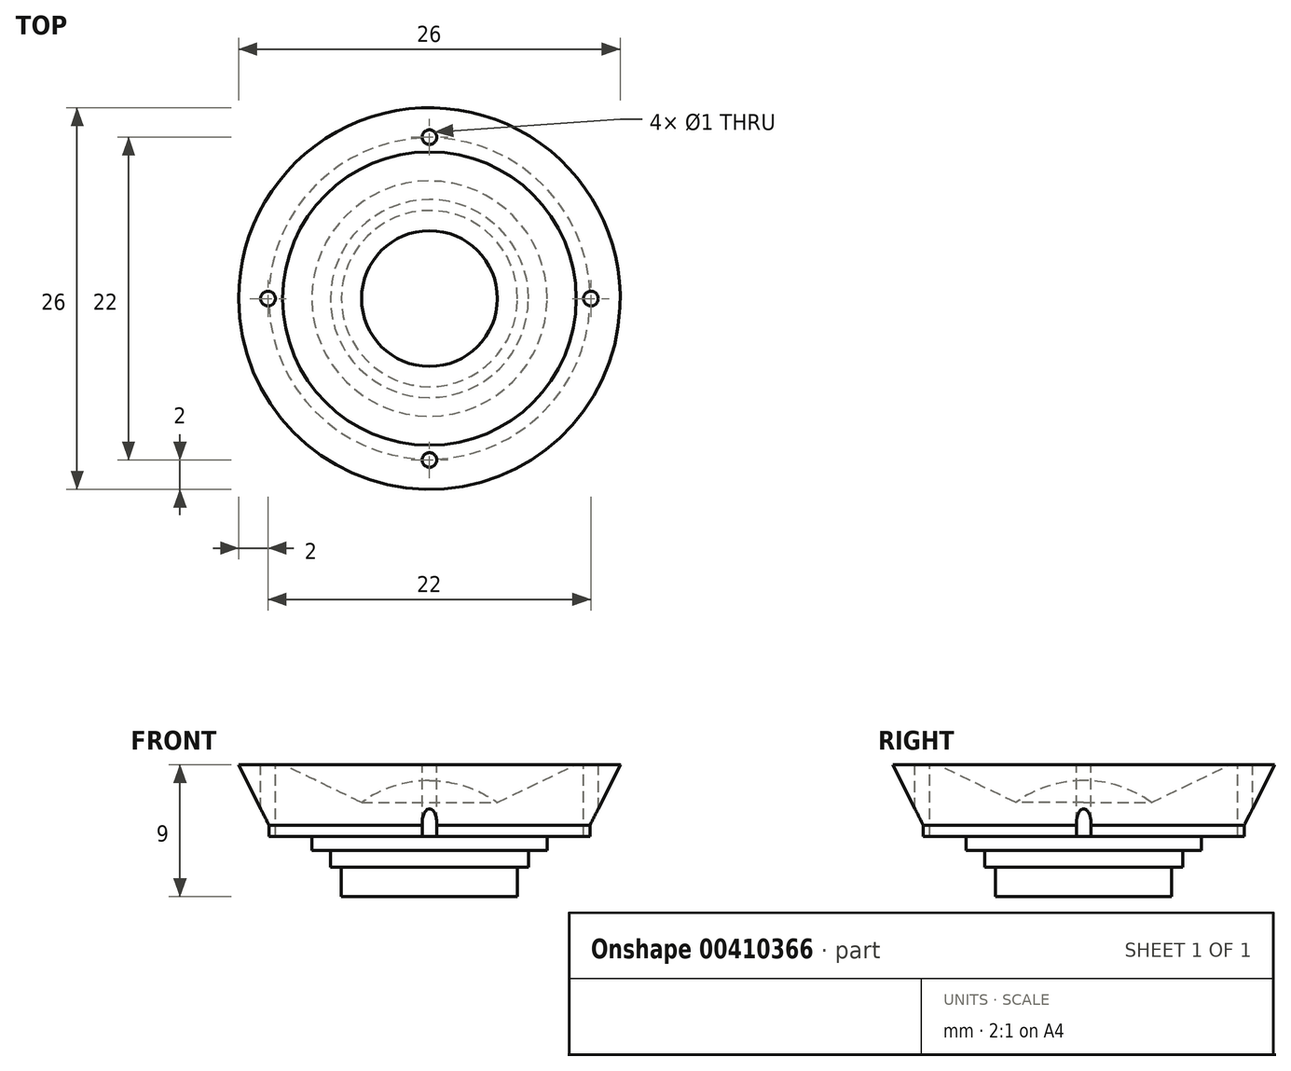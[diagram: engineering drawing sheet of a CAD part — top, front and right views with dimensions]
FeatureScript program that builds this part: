
annotation { "Feature Type Name" : "Feature", "Feature Type Description" : "" }
export const myFeature = defineFeature(function(context is Context, id is Id, definition is map)
    precondition{}
    {
        {
            var Q0;
            Q0=qCreatedBy(makeId("Front.planeOp"),FACE);
            var sketch = newSketch(context, id + "F0", { "sketchPlane" : qUnion([Q0])});
            skLineSegment(sketch, "E0", {"start": v(0, 0) * mm, "end": v(6, 0) * mm});
            skLineSegment(sketch, "E1", {"start": v(6.75, 2) * mm, "end": v(6, 2) * mm});
            skLineSegment(sketch, "E2", {"start": v(6, 2) * mm, "end": v(6, 0) * mm});
            skLineSegment(sketch, "E3", {"start": v(10, 9) * mm, "end": v(4.63, 6.4) * mm});
            skArc(sketch, "E4", {"start": v(4.63, 6.4) * mm, "mid": v(2.43, 7.52) * mm, "end": v(0, 7.9) * mm});
            skLineSegment(sketch, "E5", {"start": v(0, 0) * mm, "end": v(0, 7.9) * mm});
            skLineSegment(sketch, "E6", {"start": v(10.95, 4.87) * mm, "end": v(10.95, 4.11) * mm});
            skLineSegment(sketch, "E7", {"start": v(10.95, 4.11) * mm, "end": v(8.01, 4.11) * mm});
            skLineSegment(sketch, "E8", {"start": v(8.01, 4.11) * mm, "end": v(8.01, 3.16) * mm});
            skLineSegment(sketch, "E9", {"start": v(8.01, 3.16) * mm, "end": v(6.75, 3.16) * mm});
            skLineSegment(sketch, "E10", {"start": v(6.75, 3.16) * mm, "end": v(6.75, 2) * mm});
            skLineSegment(sketch, "E11", {"start": v(13, 9) * mm, "end": v(10, 9) * mm});
            skLineSegment(sketch, "E12", {"start": v(13, 9) * mm, "end": v(10.95, 4.87) * mm});
            skSolve(sketch);
        }
        {
            var Q0;
            Q0=makeQuery(id+"F0.imprint","IMPRINT",FACE,{"disambiguationData":[TD([[makeQuery(id+"F0.imprint","IMPRINT",EDGE,{"derivedFrom":sQuery(id+"F0.wireOp",EDGE,"E0")}),1.0]])]});
            var Q1;
            Q1=sQuery(id+"F0.wireOp",EDGE,"E5");
            revolve(context, id + "F1", {"entities" : qUnion([Q0]), "axis" : qUnion([Q1]), "revolveType" : RevolveType.FULL});
        }
        {
            var Q0;
            Q0=makeQuery(id+"F1.opRevolve","SWEPT_FACE",FACE,{"disambiguationData":[OSD([sQuery(id+"F0.wireOp",EDGE,"E11")])]});
            var sketch = newSketch(context, id + "F2", { "sketchPlane" : qUnion([Q0])});
            skCircle(sketch, "E13", {"center": v(0, 11) * mm, "radius": 0.5 * mm});
            skCircle(sketch, "E14.1.0", {"center": v(-11, 0) * mm, "radius": 0.5 * mm});
            skCircle(sketch, "E14.2.0", {"center": v(0, -11) * mm, "radius": 0.5 * mm});
            skCircle(sketch, "E14.3.0", {"center": v(11, 0) * mm, "radius": 0.5 * mm});
            skPoint(sketch, "E14.center", {"position": v(0, 0) * mm});
            skCircle(sketch, "E15", {"center": v(0, 0) * mm, "radius": 11 * mm, "construction": true});
            skSolve(sketch);
        }
        {
            var Q0;
            Q0 = qSketchRegion(id + "F2", true);
            var Q1;
            Q1 = qConstructionFilter(qBodyType(qCreatedBy(id + "F2" ,EDGE), BodyType.WIRE), ConstructionObject.NO);
            extrude(context, id + "F3", {"entities" : qUnion([Q0]), "operationType" : NewBodyOperationType.REMOVE, "surfaceEntities" : qUnion([Q1]), "endBound" : BoundingType.THROUGH_ALL, "oppositeDirection" : true, "depth" : 25 * mm});
        }
    });
